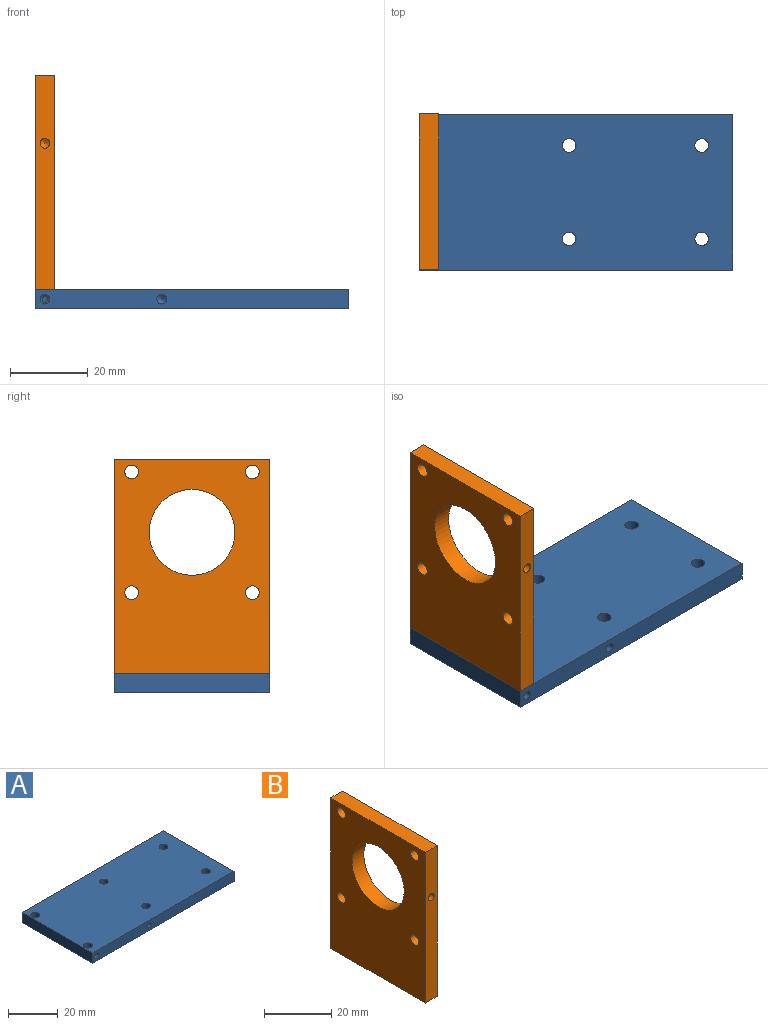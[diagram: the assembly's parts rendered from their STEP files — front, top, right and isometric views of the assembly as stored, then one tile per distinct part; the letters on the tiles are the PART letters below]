
ASSEMBLY  parts=2 mates=1
PART A: 20 faces, bbox 80.5x40x5 mm
  f0: cone r=0mm half-angle=59deg, axis (0,1,0), area 3.8mm2, adj f12,f19
  f1: cone r=0mm half-angle=59deg, axis (0,-1,0), area 3.8mm2, adj f15,f18
  f2: plane 80.5x5mm, normal (0,1,0), area 392.7mm2, adj f3,f5,f6,f7,f12,f14
  f3: plane 80.5x40mm, normal (0,0,1), area 3162.3mm2, adj f2,f4,f5,f6,f8,f9,f10,f11
  f4: plane 80.5x5mm, normal (0,-1,0), area 392.7mm2, adj f3,f5,f6,f7,f15,f17
  f5: plane 40x5mm, normal (1,0,0), area 200mm2, adj f2,f3,f4,f7
  f6: plane 40x5mm, normal (-1,0,0), area 200mm2, adj f2,f3,f4,f7
  f7: plane 80.5x40mm, normal (0,0,-1), area 3162.3mm2, adj f2,f4,f5,f6,f8,f9,f10,f11
  f8: cylinder r=1.75mm len=5mm, axis (0,0,-1), area 55mm2, adj f3,f7
  f9: cylinder r=1.75mm len=5mm, axis (0,0,-1), area 55mm2, adj f3,f7
  f10: cylinder r=1.75mm len=5mm, axis (0,0,-1), area 55mm2, adj f3,f7
  f11: cylinder r=1.75mm len=5mm, axis (0,0,-1), area 55mm2, adj f3,f7
  f12: cylinder r=1.25mm len=3mm, axis (0,1,0), area 23.6mm2, adj f0,f2
  f13: cone r=0mm half-angle=59deg, axis (0,1,0), area 5.7mm2, adj f14
  f14: cylinder r=1.25mm len=3mm, axis (0,1,0), area 23.6mm2, adj f2,f13
  f15: cylinder r=1.25mm len=3mm, axis (0,-1,0), area 23.6mm2, adj f1,f4
  f16: cone r=0mm half-angle=59deg, axis (0,-1,0), area 5.7mm2, adj f17
  f17: cylinder r=1.25mm len=3mm, axis (0,-1,0), area 23.6mm2, adj f4,f16
  f18: cylinder r=1.75mm len=5mm, axis (0,0,-1), area 53.3mm2, adj f1,f3,f7
  f19: cylinder r=1.75mm len=5mm, axis (0,0,-1), area 53.3mm2, adj f0,f3,f7
PART B: 19 faces, bbox 5x40x55 mm
  f0: plane 55x5mm, normal (0,-1,0), area 270.1mm2, adj f1,f3,f4,f13,f14
  f1: plane 55x40mm, normal (-1,0,0), area 1780.5mm2, adj f0,f2,f4,f5,f6,f7,f8,f9
  f2: plane 55x5mm, normal (0,1,0), area 270.1mm2, adj f1,f3,f4,f11,f14
  f3: plane 55x40mm, normal (1,0,0), area 1780.5mm2, adj f0,f2,f4,f5,f6,f7,f8,f9
  f4: plane 40x5mm, normal (0,0,1), area 200mm2, adj f0,f1,f2,f3
  f5: cylinder r=11.01mm len=22.03mm, axis (-1,0,0), area 346mm2, adj f1,f3
  f6: cylinder r=1.75mm len=5mm, axis (-1,0,0), area 55mm2, adj f1,f3
  f7: cylinder r=1.75mm len=5mm, axis (-1,0,0), area 55mm2, adj f1,f3
  f8: cylinder r=1.75mm len=5mm, axis (-1,0,0), area 55mm2, adj f1,f3
  f9: cylinder r=1.75mm len=5mm, axis (-1,0,0), area 55mm2, adj f1,f3
  f10: cone r=0mm half-angle=59deg, axis (0,1,0), area 5.7mm2, adj f11
  f11: cylinder r=1.25mm len=3mm, axis (0,1,0), area 23.6mm2, adj f2,f10
  f12: cone r=0mm half-angle=59deg, axis (0,-1,0), area 5.7mm2, adj f13
  f13: cylinder r=1.25mm len=3mm, axis (0,-1,0), area 23.6mm2, adj f0,f12
  f14: plane 40x5mm, normal (0,0,-1), area 190.2mm2, adj f0,f1,f2,f3,f16,f18
  f15: cone r=0mm half-angle=59deg, axis (0,0,-1), area 5.7mm2, adj f16
  f16: cylinder r=1.25mm len=10mm, axis (0,0,-1), area 78.5mm2, adj f14,f15
  f17: cone r=0mm half-angle=59deg, axis (0,0,-1), area 5.7mm2, adj f18
  f18: cylinder r=1.25mm len=10mm, axis (0,0,-1), area 78.5mm2, adj f14,f17
PLACE A at identity
PLACE B at identity
MATE fastened B.f15 <-> A.f19  axis (0,0,-1) through (-37.75,15,5)mm
